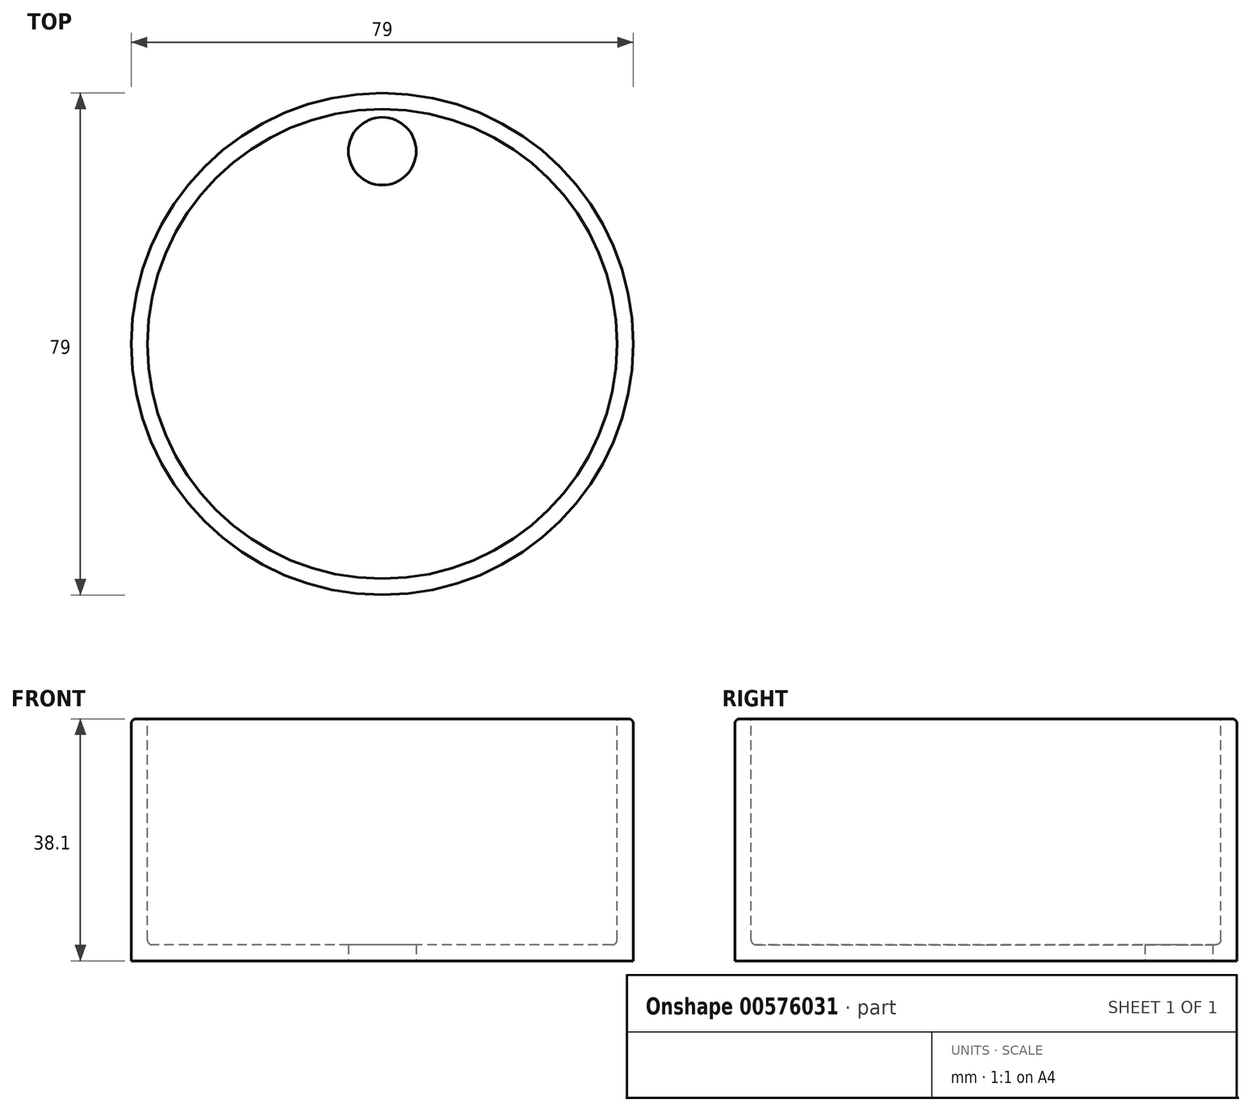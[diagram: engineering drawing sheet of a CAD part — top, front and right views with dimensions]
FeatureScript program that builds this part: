
annotation { "Feature Type Name" : "Feature", "Feature Type Description" : "" }
export const myFeature = defineFeature(function(context is Context, id is Id, definition is map)
    precondition{}
    {
        {
            var Q0;
            Q0=qCreatedBy(makeId("Top.planeOp"),FACE);
            var sketch = newSketch(context, id + "F0", { "sketchPlane" : qUnion([Q0])});
            skCircle(sketch, "E0", {"center": v(0, 0) * mm, "radius": 39.5 * mm});
            skSolve(sketch);
        }
        {
            var Q0;
            Q0 = qSketchRegion(id + "F0", true);
            extrude(context, id + "F1", {"entities" : qUnion([Q0]), "depth" : 38.1 * mm, "offsetDistance" : 25.4 * mm});
        }
        {
            var Q0;
            Q0=makeQuery(id+"F1.opExtrude","CAP_FACE",FACE,{"disambiguationData":[OSD([sQuery(id+"F0.wireOp",EDGE,"E0")])],"isStart":false});
            var sketch = newSketch(context, id + "F2", { "sketchPlane" : qUnion([Q0])});
            skCircle(sketch, "E1.0", {"center": v(0, 0) * mm, "radius": 36.96 * mm});
            skSolve(sketch);
        }
        {
            var Q0;
            Q0 = qSketchRegion(id + "F2", true);
            extrude(context, id + "F3", {"entities" : qUnion([Q0]), "operationType" : NewBodyOperationType.REMOVE, "oppositeDirection" : true, "depth" : 35.56 * mm, "offsetDistance" : 25.4 * mm});
        }
        {
            var Q0;
            Q0=makeQuery(id+"F3.boolean.opBoolean","COPY",EDGE,{"derivedFrom":makeQuery(id+"F3.opExtrude","CAP_EDGE",EDGE,{"disambiguationData":[OSD([sQuery(id+"F2.wireOp",EDGE,"E1.0")])],"isStart":false})});
            fillet(context, id + "F4", {"entities" : qUnion([Q0]), "radius" : 0.76 * mm, "tangentPropagation" : true, "allowEdgeOverflow" : false});
        }
        {
            var Q0;
            Q0=makeQuery(id+"F1.opExtrude","CAP_EDGE",EDGE,{"disambiguationData":[OSD([sQuery(id+"F0.wireOp",EDGE,"E0")])],"isStart":false});
            fillet(context, id + "F5", {"entities" : qUnion([Q0]), "radius" : 0.76 * mm, "tangentPropagation" : true, "allowEdgeOverflow" : false});
        }
        {
            var Q0;
            Q0=makeQuery(id+"F1.opExtrude","CAP_FACE",FACE,{"disambiguationData":[OSD([sQuery(id+"F0.wireOp",EDGE,"E0")])],"isStart":true});
            var sketch = newSketch(context, id + "F6", { "sketchPlane" : qUnion([Q0])});
            skLineSegment(sketch, "E2", {"start": v(0, 0) * mm, "end": v(0, -39.5) * mm});
            skLineSegment(sketch, "E3", {"start": v(0, -39.5) * mm, "end": v(0, -36.96) * mm});
            skLineSegment(sketch, "E4", {"start": v(0, -36.96) * mm, "end": v(0, -30.35) * mm});
            skCircle(sketch, "E5", {"center": v(0, -30.35) * mm, "radius": 5.33 * mm});
            skLineSegment(sketch, "E6", {"start": v(0, -36.96) * mm, "end": v(0, -35.69) * mm});
            skSolve(sketch);
        }
        {
            var Q0;
            Q0 = qSketchRegion(id + "F6", true);
            extrude(context, id + "F7", {"entities" : qUnion([Q0]), "operationType" : NewBodyOperationType.REMOVE, "oppositeDirection" : true, "depth" : 25.4 * mm, "offsetDistance" : 25.4 * mm});
        }
    });
